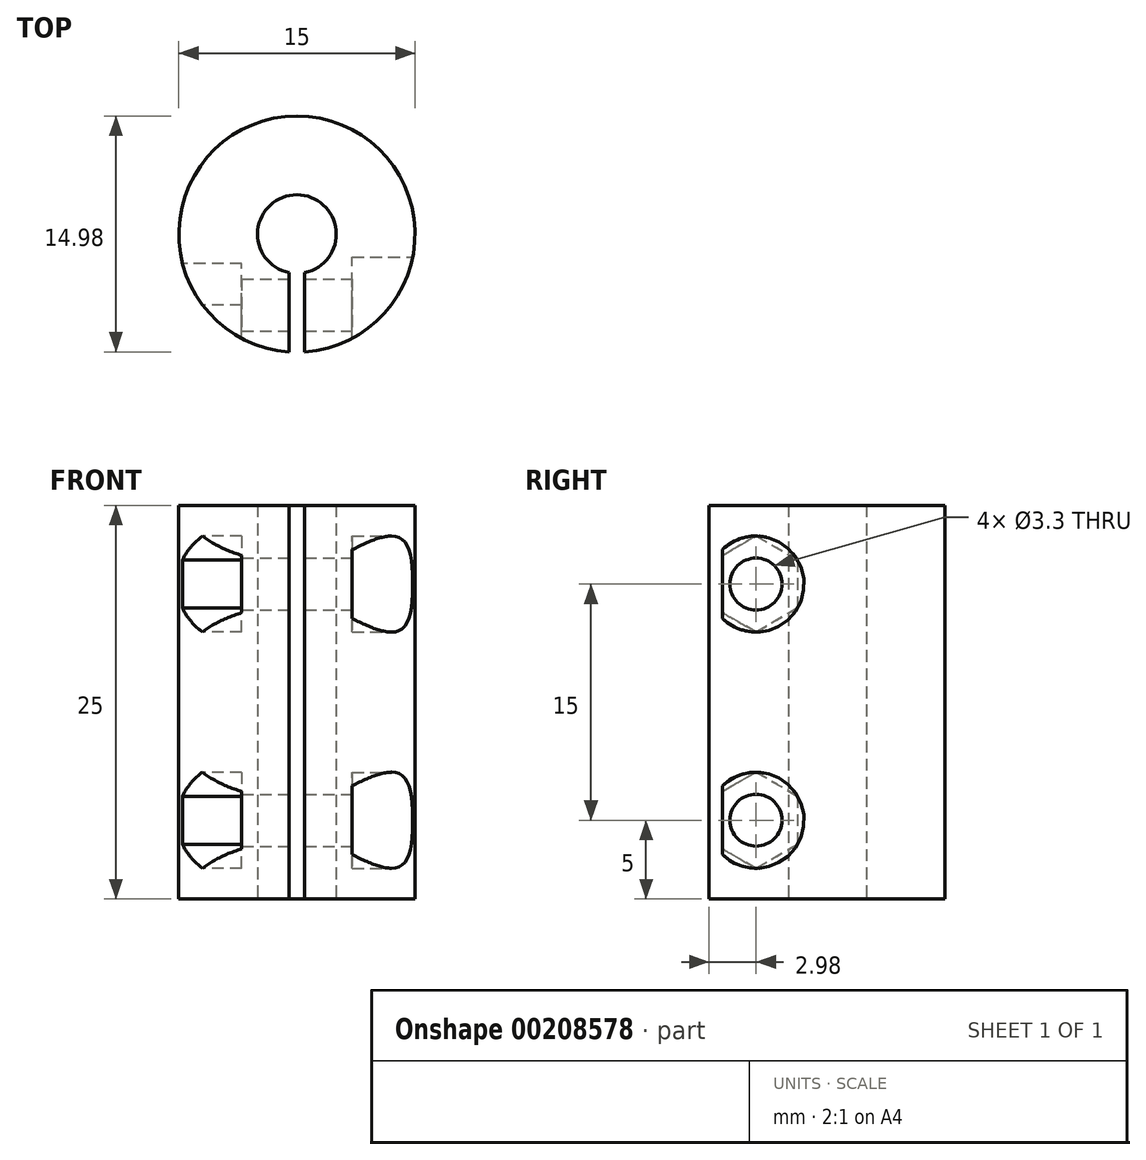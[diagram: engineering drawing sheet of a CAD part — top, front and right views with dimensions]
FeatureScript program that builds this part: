
annotation { "Feature Type Name" : "Feature", "Feature Type Description" : "" }
export const myFeature = defineFeature(function(context is Context, id is Id, definition is map)
    precondition{}
    {
        {
            var Q0;
            Q0=qCreatedBy(makeId("Top.planeOp"),FACE);
            var sketch = newSketch(context, id + "F0", { "sketchPlane" : qUnion([Q0])});
            skCircle(sketch, "E0", {"center": v(0, 0) * mm, "radius": 2.5 * mm});
            skCircle(sketch, "E1", {"center": v(0, 0) * mm, "radius": 7.5 * mm});
            skLineSegment(sketch, "E2", {"start": v(0, 0) * mm, "end": v(7.5, 0) * mm, "construction": true});
            skLineSegment(sketch, "E3", {"start": v(-7.5, 0) * mm, "end": v(0, 0) * mm, "construction": true});
            skLineSegment(sketch, "E4", {"start": v(0, 0) * mm, "end": v(0, -12.1) * mm, "construction": true});
            skLineSegment(sketch, "E5", {"start": v(-0.5, -2.45) * mm, "end": v(-0.5, -7.48) * mm});
            skLineSegment(sketch, "E6", {"start": v(0.5, -2.45) * mm, "end": v(0.5, -7.48) * mm});
            skSolve(sketch);
        }
        {
            var Q0;
            {var subQ0=sQuery(id+"F0.wireOp",EDGE,"E5");Q0=makeQuery(id+"F0.imprint","IMPRINT",FACE,{"disambiguationData":[TD([[makeQuery(id+"F0.imprint","IMPRINT",EDGE,{"derivedFrom":subQ0}),-1.0]])]});}
            extrude(context, id + "F1", {"entities" : qUnion([Q0]), "depth" : 25 * mm});
        }
        {
            var Q0;
            Q0=sQuery(id+"F0.wireOp",VERTEX,"E2.end");
            var Q1;
            Q1=qCreatedBy(makeId("Right.planeOp"),FACE);
            cPlane(context, id + "F2", {"entities" : qUnion([Q0, Q1]), "cplaneType" : CPlaneType.PLANE_POINT, "offset" : 50 * mm, "width" : 150 * mm, "height" : 150 * mm});
        }
        {
            var Q0;
            Q0=qCreatedBy(id+"F2.planeOp",FACE);
            var sketch = newSketch(context, id + "F3", { "sketchPlane" : qUnion([Q0])});
            skCircle(sketch, "E7", {"center": v(-4.5, 20) * mm, "radius": 1.5 * mm});
            skCircle(sketch, "E8", {"center": v(-4.5, 5) * mm, "radius": 1.5 * mm});
            skPoint(sketch, "E9.0.midPoint", {"position": v(-3.06, 2.34) * mm});
            skSolve(sketch);
        }
        {
            var Q0;
            Q0=sQuery(id+"F3.wireOp",VERTEX,"E7.center");
            var Q1;
            Q1=sQuery(id+"F3.wireOp",VERTEX,"E8.center");
            var Q2;
            Q2=makeQuery(id+"F1.opExtrude","SWEPT_BODY",BODY,{"disambiguationData":[OSD([sQuery(id+"F0.wireOp",EDGE,"E0"),sQuery(id+"F0.wireOp",EDGE,"E1")])]});
            hole(context, id + "F4", {"style" : HoleStyle.C_BORE, "endStyle" : HoleEndStyle.THROUGH, "holeDiameter" : 3.3 * mm, "cBoreDiameter" : 6.1 * mm, "cBoreDepth" : 4 * mm, "startFromSketch" : true, "locations" : qUnion([Q0, Q1]), "scope" : qUnion([Q2]), "isTappedThrough" : true});
        }
        {
            var Q0;
            Q0=makeQuery(id+"F3.imprint","IMPRINT",FACE,{"disambiguationData":[TD([[makeQuery(id+"F3.imprint","IMPRINT",EDGE,{"derivedFrom":sQuery(id+"F3.wireOp",EDGE,"E8")}),-1.0]])]});
            var Q1;
            Q1=makeQuery(id+"F3.imprint","IMPRINT",FACE,{"disambiguationData":[TD([[makeQuery(id+"F3.imprint","IMPRINT",EDGE,{"derivedFrom":sQuery(id+"F3.wireOp",EDGE,"E8")}),1.0]])]});
            extrude(context, id + "F5", {"entities" : qUnion([Q0, Q1]), "operationType" : NewBodyOperationType.REMOVE, "oppositeDirection" : true, "depth" : 3 * mm});
        }
        {
            var Q0;
            Q0=makeQuery(id+"F3.imprint","IMPRINT",FACE,{"disambiguationData":[TD([[makeQuery(id+"F3.imprint","IMPRINT",EDGE,{"derivedFrom":sQuery(id+"F3.wireOp",EDGE,"E7")}),-1.0]])]});
            var Q1;
            Q1=makeQuery(id+"F3.imprint","IMPRINT",FACE,{"disambiguationData":[TD([[makeQuery(id+"F3.imprint","IMPRINT",EDGE,{"derivedFrom":sQuery(id+"F3.wireOp",EDGE,"E7")}),1.0]])]});
            extrude(context, id + "F6", {"entities" : qUnion([Q0, Q1]), "operationType" : NewBodyOperationType.REMOVE, "oppositeDirection" : true, "depth" : 3 * mm});
        }
        {
            var Q0;
            Q0=sQuery(id+"F0.wireOp",VERTEX,"E3.start");
            var Q1;
            Q1=qCreatedBy(id+"F2.planeOp",FACE);
            cPlane(context, id + "F7", {"entities" : qUnion([Q0, Q1]), "cplaneType" : CPlaneType.PLANE_POINT, "offset" : 25 * mm, "width" : 150 * mm, "height" : 150 * mm});
        }
        {
            var Q0;
            Q0=qCreatedBy(id+"F7.planeOp",FACE);
            var sketch = newSketch(context, id + "F8", { "sketchPlane" : qUnion([Q0])});
            skCircle(sketch, "E10.cCircle", {"center": v(-4.5, 20) * mm, "radius": 2.64 * mm, "construction": true});
            skLineSegment(sketch, "E10.0", {"start": v(-1.86, 21.53) * mm, "end": v(-1.86, 18.48) * mm});
            skLineSegment(sketch, "E10.1", {"start": v(-1.86, 18.48) * mm, "end": v(-4.5, 16.95) * mm});
            skLineSegment(sketch, "E10.2", {"start": v(-4.5, 16.95) * mm, "end": v(-7.14, 18.47) * mm});
            skLineSegment(sketch, "E10.3", {"start": v(-7.14, 18.47) * mm, "end": v(-7.14, 21.52) * mm});
            skLineSegment(sketch, "E10.4", {"start": v(-7.14, 21.52) * mm, "end": v(-4.5, 23.05) * mm});
            skLineSegment(sketch, "E10.5", {"start": v(-4.5, 23.05) * mm, "end": v(-1.86, 21.53) * mm});
            skPoint(sketch, "E10.0.midPoint", {"position": v(-1.86, 20) * mm});
            skCircle(sketch, "E11.cCircle", {"center": v(-4.5, 5) * mm, "radius": 2.64 * mm, "construction": true});
            skLineSegment(sketch, "E11.0", {"start": v(-4.5, 1.95) * mm, "end": v(-7.14, 3.48) * mm});
            skLineSegment(sketch, "E11.1", {"start": v(-7.14, 3.48) * mm, "end": v(-7.14, 6.53) * mm});
            skLineSegment(sketch, "E11.2", {"start": v(-7.14, 6.53) * mm, "end": v(-4.5, 8.05) * mm});
            skLineSegment(sketch, "E11.3", {"start": v(-4.5, 8.05) * mm, "end": v(-1.86, 6.52) * mm});
            skLineSegment(sketch, "E11.4", {"start": v(-1.86, 6.52) * mm, "end": v(-1.86, 3.47) * mm});
            skLineSegment(sketch, "E11.5", {"start": v(-1.86, 3.48) * mm, "end": v(-4.5, 1.95) * mm});
            skPoint(sketch, "E11.0.midPoint", {"position": v(-5.82, 2.71) * mm});
            skSolve(sketch);
        }
        {
            var Q0;
            Q0=makeQuery(id+"F8.imprint","IMPRINT",FACE,{"disambiguationData":[TD([[makeQuery(id+"F8.imprint","IMPRINT",EDGE,{"derivedFrom":sQuery(id+"F8.wireOp",EDGE,"E11.0")}),-1.0]])]});
            var Q1;
            Q1=makeQuery(id+"F8.imprint","IMPRINT",FACE,{"disambiguationData":[TD([[makeQuery(id+"F8.imprint","IMPRINT",EDGE,{"derivedFrom":sQuery(id+"F8.wireOp",EDGE,"E10.0")}),-1.0]])]});
            extrude(context, id + "F9", {"entities" : qUnion([Q0, Q1]), "operationType" : NewBodyOperationType.REMOVE, "depth" : 4 * mm});
        }
    });
